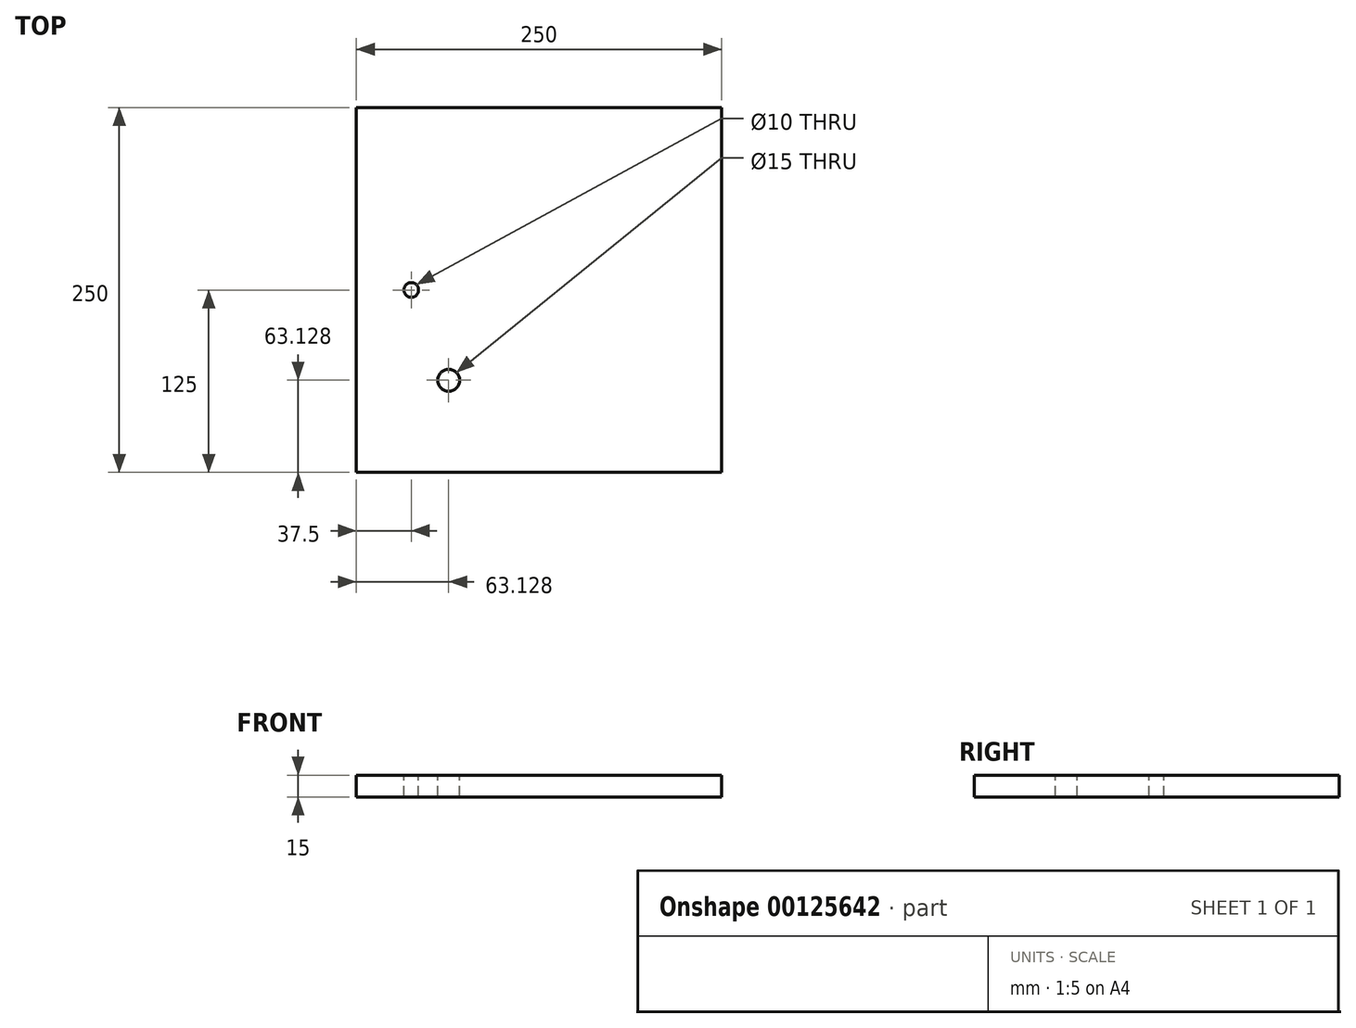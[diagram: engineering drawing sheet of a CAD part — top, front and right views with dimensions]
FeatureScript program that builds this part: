
annotation { "Feature Type Name" : "Feature", "Feature Type Description" : "" }
export const myFeature = defineFeature(function(context is Context, id is Id, definition is map)
    precondition{}
    {
        {
            var Q0;
            Q0=qCreatedBy(makeId("Top.planeOp"),FACE);
            var sketch = newSketch(context, id + "F0", { "sketchPlane" : qUnion([Q0])});
            skLineSegment(sketch, "E0.bottom", {"start": v(-250, 250) * mm, "end": v(0, 250) * mm});
            skLineSegment(sketch, "E0.top", {"start": v(-250, 0) * mm, "end": v(0, 0) * mm});
            skLineSegment(sketch, "E0.left", {"start": v(-250, 250) * mm, "end": v(-250, 0) * mm});
            skLineSegment(sketch, "E0.right", {"start": v(0, 250) * mm, "end": v(0, 0) * mm});
            skSolve(sketch);
        }
        {
            var Q0;
            Q0 = qSketchRegion(id + "F0", true);
            extrude(context, id + "F1", {"entities" : qUnion([Q0]), "depth" : 15 * mm});
        }
        {
            var Q0;
            Q0=makeQuery(id+"F1.opExtrude","SWEPT_FACE",FACE,{"disambiguationData":[OSD([sQuery(id+"F0.wireOp",EDGE,"E0.left")])]});
            var Q1;
            Q1=makeQuery(id+"F1.opExtrude","SWEPT_FACE",FACE,{"disambiguationData":[OSD([sQuery(id+"F0.wireOp",EDGE,"E0.right")])]});
            cPlane(context, id + "F2", {"entities" : qUnion([Q0, Q1]), "cplaneType" : CPlaneType.MID_PLANE, "offset" : 25 * mm, "width" : 150 * mm, "height" : 150 * mm});
        }
        {
            var Q0;
            Q0=makeQuery(id+"F1.opExtrude","SWEPT_FACE",FACE,{"disambiguationData":[OSD([sQuery(id+"F0.wireOp",EDGE,"E0.top")])]});
            var Q1;
            Q1=makeQuery(id+"F1.opExtrude","SWEPT_FACE",FACE,{"disambiguationData":[OSD([sQuery(id+"F0.wireOp",EDGE,"E0.bottom")])]});
            cPlane(context, id + "F3", {"entities" : qUnion([Q0, Q1]), "cplaneType" : CPlaneType.MID_PLANE, "offset" : 25 * mm, "width" : 150 * mm, "height" : 150 * mm});
        }
        {
            var Q0;
            Q0=qCreatedBy(id+"F3.planeOp",FACE);
            var sketch = newSketch(context, id + "F4", { "sketchPlane" : qUnion([Q0])});
            skLineSegment(sketch, "E1", {"start": v(-125, 26.5) * mm, "end": v(-125, -13.86) * mm, "construction": true});
            skSolve(sketch);
        }
        {
            var Q0;
            Q0=makeQuery(id+"F1.opExtrude","CAP_FACE",FACE,{"disambiguationData":[OSD([sQuery(id+"F0.wireOp",EDGE,"E0.bottom"),sQuery(id+"F0.wireOp",EDGE,"E0.top"),sQuery(id+"F0.wireOp",EDGE,"E0.left"),sQuery(id+"F0.wireOp",EDGE,"E0.right")])],"isStart":false});
            var sketch = newSketch(context, id + "F5", { "sketchPlane" : qUnion([Q0])});
            skCircle(sketch, "E2", {"center": v(-212.5, 125) * mm, "radius": 5 * mm});
            skSolve(sketch);
        }
        {
            var Q0;
            Q0 = qSketchRegion(id + "F5", true);
            extrude(context, id + "F6", {"entities" : qUnion([Q0]), "operationType" : NewBodyOperationType.REMOVE, "endBound" : BoundingType.THROUGH_ALL, "oppositeDirection" : true, "depth" : 25 * mm});
        }
        {
            var Q0;
            Q0=qCreatedBy(id+"F3.planeOp",FACE);
            var Q1;
            Q1=qCreatedBy(id+"F2.planeOp",FACE);
            cPlane(context, id + "F7", {"entities" : qUnion([Q0, Q1]), "cplaneType" : CPlaneType.MID_PLANE, "offset" : 25 * mm, "width" : 150 * mm, "height" : 150 * mm});
        }
        {
            var Q0;
            Q0=makeQuery(id+"F1.opExtrude","CAP_FACE",FACE,{"disambiguationData":[OSD([sQuery(id+"F0.wireOp",EDGE,"E0.bottom"),sQuery(id+"F0.wireOp",EDGE,"E0.top"),sQuery(id+"F0.wireOp",EDGE,"E0.left"),sQuery(id+"F0.wireOp",EDGE,"E0.right")])],"isStart":false});
            var sketch = newSketch(context, id + "F8", { "sketchPlane" : qUnion([Q0])});
            skCircle(sketch, "E3", {"center": v(-186.87, 63.13) * mm, "radius": 7.5 * mm});
            skSolve(sketch);
        }
        {
            var Q0;
            Q0 = qSketchRegion(id + "F8", true);
            extrude(context, id + "F9", {"entities" : qUnion([Q0]), "operationType" : NewBodyOperationType.REMOVE, "endBound" : BoundingType.THROUGH_ALL, "oppositeDirection" : true, "depth" : 25 * mm});
        }
    });
